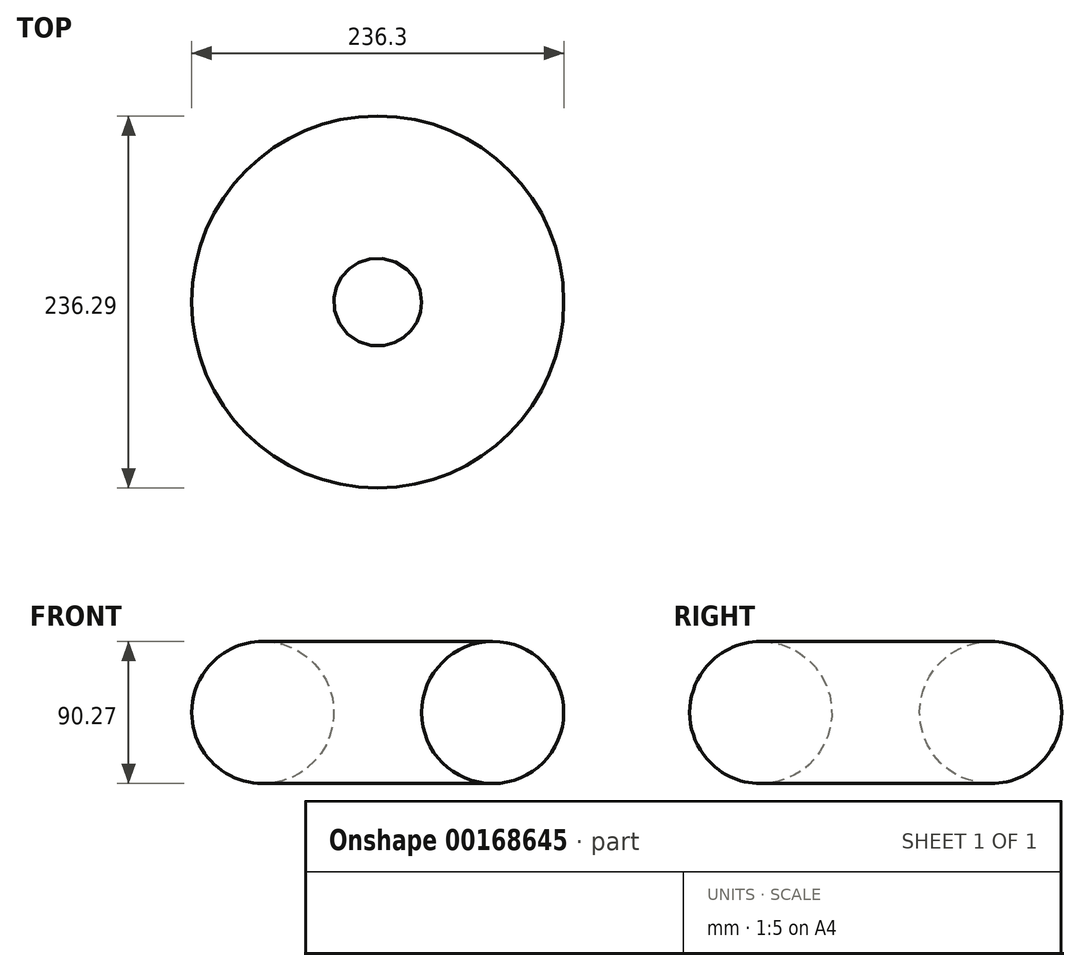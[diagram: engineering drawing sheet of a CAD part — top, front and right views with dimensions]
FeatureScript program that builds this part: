
annotation { "Feature Type Name" : "Feature", "Feature Type Description" : "" }
export const myFeature = defineFeature(function(context is Context, id is Id, definition is map)
    precondition{}
    {
        {
            var Q0;
            Q0=qCreatedBy(makeId("Right.planeOp"),FACE);
            var sketch = newSketch(context, id + "F0", { "sketchPlane" : qUnion([Q0])});
            skCircle(sketch, "E0", {"center": v(-11.47, 18.33) * mm, "radius": 45.14 * mm});
            skLineSegment(sketch, "E1", {"start": v(61.53, 65.4) * mm, "end": v(61.53, -68.69) * mm, "construction": true});
            skSolve(sketch);
        }
        {
            var Q0;
            Q0=makeQuery(id+"F0.imprint","IMPRINT",FACE,{"disambiguationData":[TD([[makeQuery(id+"F0.imprint","IMPRINT",EDGE,{"derivedFrom":sQuery(id+"F0.wireOp",EDGE,"E0")}),1.0]])]});
            var Q1;
            Q1=sQuery(id+"F0.wireOp",EDGE,"E1");
            revolve(context, id + "F1", {"entities" : qUnion([Q0]), "axis" : qUnion([Q1]), "revolveType" : RevolveType.FULL});
        }
    });
